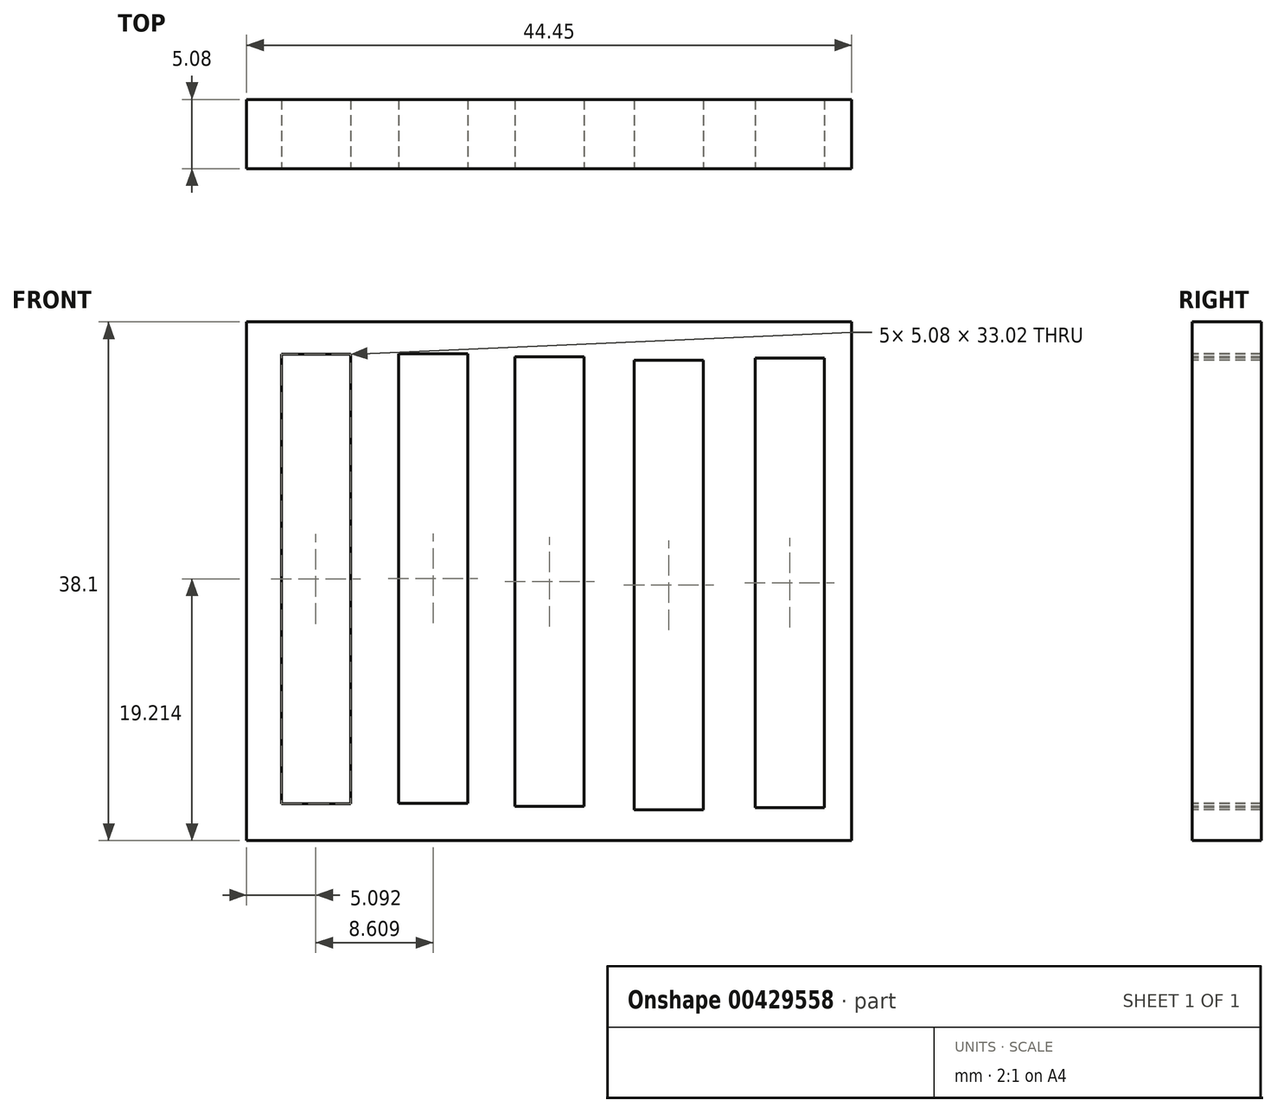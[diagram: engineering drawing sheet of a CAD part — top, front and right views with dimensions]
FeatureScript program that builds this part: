
annotation { "Feature Type Name" : "Feature", "Feature Type Description" : "" }
export const myFeature = defineFeature(function(context is Context, id is Id, definition is map)
    precondition{}
    {
        {
            var Q0;
            Q0=qCreatedBy(makeId("Front.planeOp"),FACE);
            var sketch = newSketch(context, id + "F0", { "sketchPlane" : qUnion([Q0])});
            skLineSegment(sketch, "E0.bottom", {"start": v(-19.72, 0) * mm, "end": v(24.73, 0) * mm});
            skLineSegment(sketch, "E0.top", {"start": v(-19.72, 38.1) * mm, "end": v(24.73, 38.1) * mm});
            skLineSegment(sketch, "E0.left", {"start": v(-19.72, 0) * mm, "end": v(-19.72, 38.1) * mm});
            skLineSegment(sketch, "E0.right", {"start": v(24.73, 0) * mm, "end": v(24.73, 38.1) * mm});
            skSolve(sketch);
        }
        {
            var Q0;
            Q0 = qSketchRegion(id + "F0", true);
            extrude(context, id + "F1", {"entities" : qUnion([Q0]), "depth" : 5.08 * mm});
        }
        {
            var Q0;
            Q0=makeQuery(id+"F1.opExtrude","CAP_FACE",FACE,{"disambiguationData":[OSD([sQuery(id+"F0.wireOp",EDGE,"E0.bottom"),sQuery(id+"F0.wireOp",EDGE,"E0.top"),sQuery(id+"F0.wireOp",EDGE,"E0.left"),sQuery(id+"F0.wireOp",EDGE,"E0.right")])],"isStart":false});
            var sketch = newSketch(context, id + "F2", { "sketchPlane" : qUnion([Q0])});
            skLineSegment(sketch, "E1.bottom", {"start": v(-17.17, 35.72) * mm, "end": v(-12.09, 35.72) * mm});
            skLineSegment(sketch, "E1.top", {"start": v(-17.17, 2.7) * mm, "end": v(-12.09, 2.7) * mm});
            skLineSegment(sketch, "E1.left", {"start": v(-17.17, 35.72) * mm, "end": v(-17.17, 2.7) * mm});
            skLineSegment(sketch, "E1.right", {"start": v(-12.09, 35.72) * mm, "end": v(-12.09, 2.7) * mm});
            skLineSegment(sketch, "E2.bottom", {"start": v(-8.56, 35.77) * mm, "end": v(-3.48, 35.77) * mm});
            skLineSegment(sketch, "E2.top", {"start": v(-8.56, 2.75) * mm, "end": v(-3.48, 2.75) * mm});
            skLineSegment(sketch, "E2.left", {"start": v(-8.56, 35.77) * mm, "end": v(-8.56, 2.75) * mm});
            skLineSegment(sketch, "E2.right", {"start": v(-3.48, 35.77) * mm, "end": v(-3.48, 2.75) * mm});
            skLineSegment(sketch, "E3.bottom", {"start": v(0, 35.53) * mm, "end": v(5.08, 35.53) * mm});
            skLineSegment(sketch, "E3.top", {"start": v(0, 2.5) * mm, "end": v(5.08, 2.5) * mm});
            skLineSegment(sketch, "E3.left", {"start": v(0, 35.53) * mm, "end": v(0, 2.5) * mm});
            skLineSegment(sketch, "E3.right", {"start": v(5.08, 35.53) * mm, "end": v(5.08, 2.5) * mm});
            skLineSegment(sketch, "E4.bottom", {"start": v(8.75, 35.27) * mm, "end": v(13.83, 35.27) * mm});
            skLineSegment(sketch, "E4.top", {"start": v(8.75, 2.25) * mm, "end": v(13.83, 2.25) * mm});
            skLineSegment(sketch, "E4.left", {"start": v(8.75, 35.27) * mm, "end": v(8.75, 2.25) * mm});
            skLineSegment(sketch, "E4.right", {"start": v(13.83, 35.27) * mm, "end": v(13.83, 2.25) * mm});
            skLineSegment(sketch, "E5.bottom", {"start": v(17.64, 35.45) * mm, "end": v(22.72, 35.45) * mm});
            skLineSegment(sketch, "E5.top", {"start": v(17.64, 2.43) * mm, "end": v(22.72, 2.43) * mm});
            skLineSegment(sketch, "E5.left", {"start": v(17.64, 35.45) * mm, "end": v(17.64, 2.43) * mm});
            skLineSegment(sketch, "E5.right", {"start": v(22.72, 35.45) * mm, "end": v(22.72, 2.43) * mm});
            skSolve(sketch);
        }
        {
            var Q0;
            Q0 = qSketchRegion(id + "F2", true);
            extrude(context, id + "F3", {"entities" : qUnion([Q0]), "operationType" : NewBodyOperationType.REMOVE, "oppositeDirection" : true, "depth" : 25.4 * mm});
        }
    });
